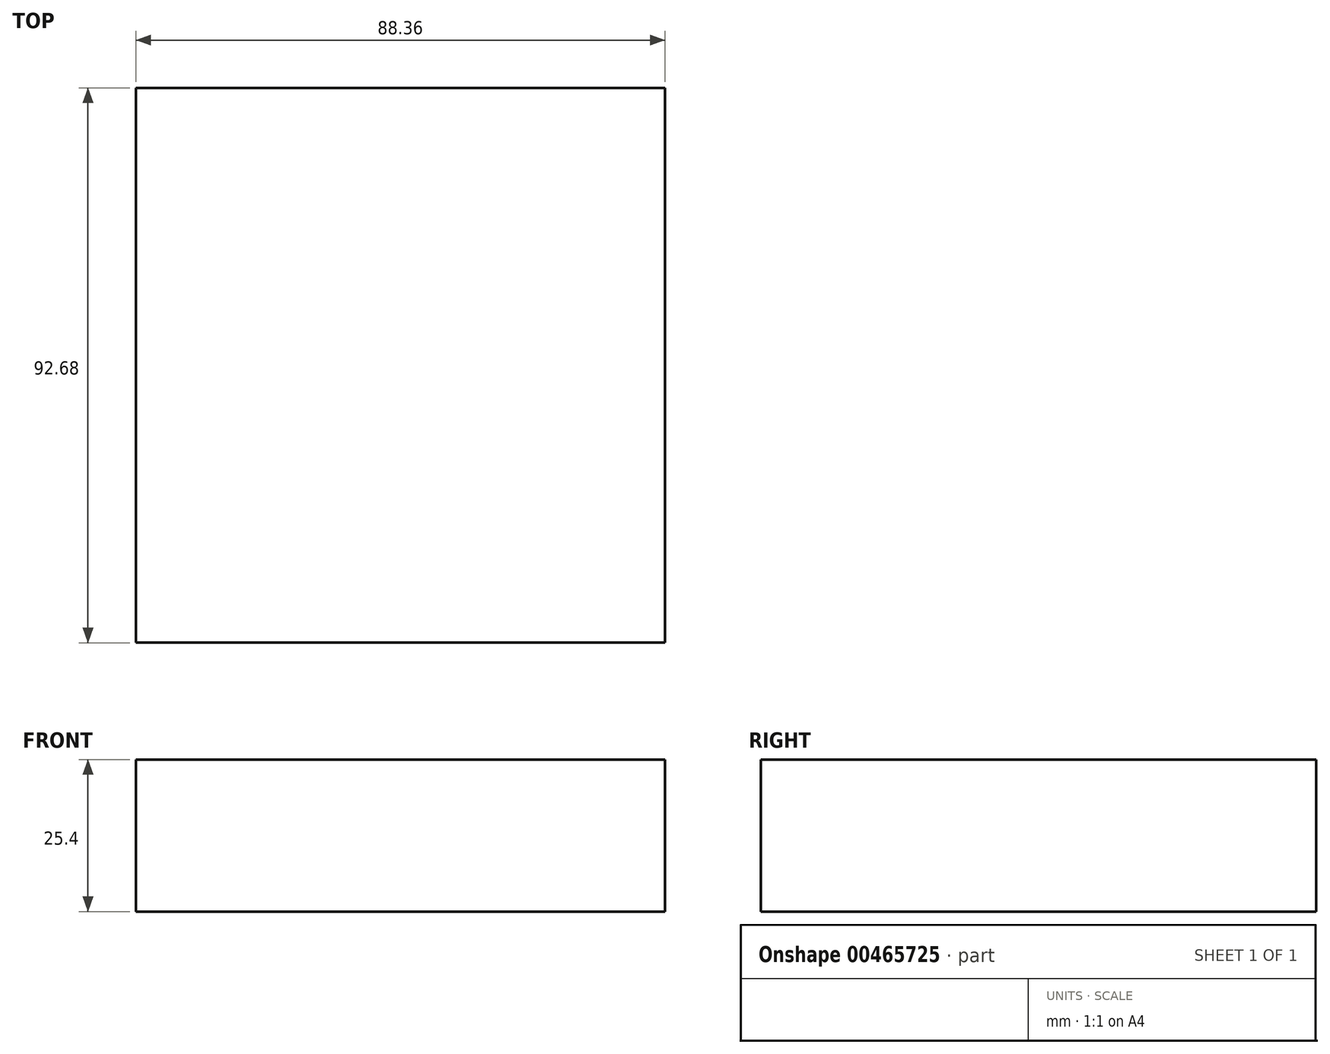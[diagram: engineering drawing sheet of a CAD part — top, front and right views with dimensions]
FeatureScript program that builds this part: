
annotation { "Feature Type Name" : "Feature", "Feature Type Description" : "" }
export const myFeature = defineFeature(function(context is Context, id is Id, definition is map)
    precondition{}
    {
        {
            var Q0;
            Q0=qCreatedBy(makeId("Top.planeOp"),FACE);
            var sketch = newSketch(context, id + "F0", { "sketchPlane" : qUnion([Q0])});
            skLineSegment(sketch, "E0.bottom", {"start": v(40.58, 51.52) * mm, "end": v(-47.78, 51.52) * mm});
            skLineSegment(sketch, "E0.top", {"start": v(40.58, -41.16) * mm, "end": v(-47.78, -41.16) * mm});
            skLineSegment(sketch, "E0.left", {"start": v(40.58, 51.52) * mm, "end": v(40.58, -41.16) * mm});
            skLineSegment(sketch, "E0.right", {"start": v(-47.78, 51.52) * mm, "end": v(-47.78, -41.16) * mm});
            skSolve(sketch);
        }
        {
            var Q0;
            Q0=makeQuery(id+"F0.imprint","IMPRINT",FACE,{"disambiguationData":[TD([[makeQuery(id+"F0.imprint","IMPRINT",EDGE,{"derivedFrom":sQuery(id+"F0.wireOp",EDGE,"E0.bottom")}),1.0]])]});
            extrude(context, id + "F1", {"entities" : qUnion([Q0]), "depth" : 25.4 * mm});
        }
    });
